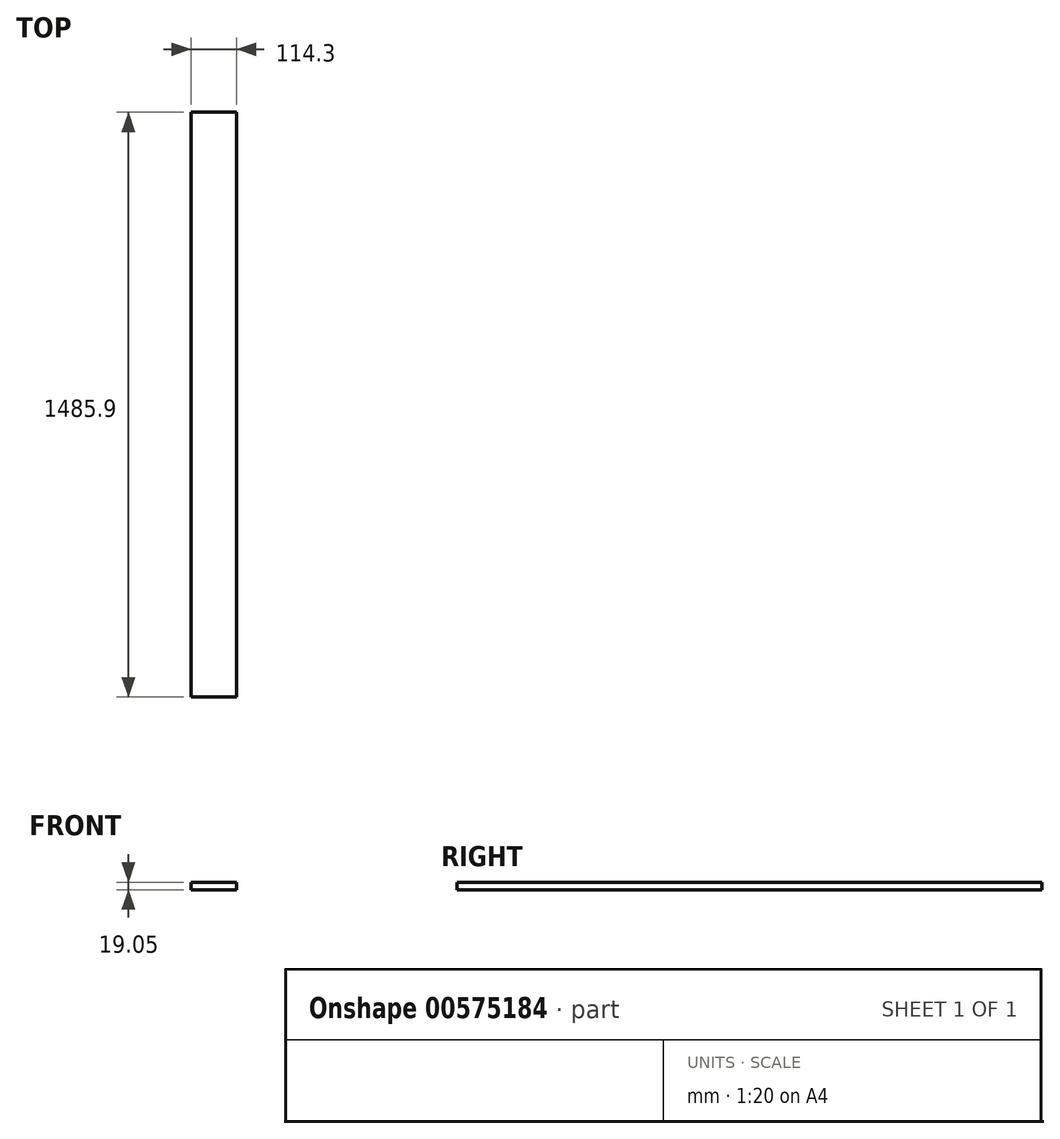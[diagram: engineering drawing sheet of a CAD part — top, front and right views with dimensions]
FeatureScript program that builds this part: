
annotation { "Feature Type Name" : "Feature", "Feature Type Description" : "" }
export const myFeature = defineFeature(function(context is Context, id is Id, definition is map)
    precondition{}
    {
        {
            var Q0;
            Q0=qCreatedBy(makeId("Top.planeOp"),FACE);
            var sketch = newSketch(context, id + "F0", { "sketchPlane" : qUnion([Q0])});
            skLineSegment(sketch, "E0.bottom", {"start": v(57.15, 742.95) * mm, "end": v(-57.15, 742.95) * mm});
            skLineSegment(sketch, "E0.top", {"start": v(57.15, -742.95) * mm, "end": v(-57.15, -742.95) * mm});
            skLineSegment(sketch, "E0.left", {"start": v(57.15, 742.95) * mm, "end": v(57.15, -742.95) * mm});
            skLineSegment(sketch, "E0.right", {"start": v(-57.15, 742.95) * mm, "end": v(-57.15, -742.95) * mm});
            skPoint(sketch, "E0.middle", {"position": v(0, 0) * mm});
            skSolve(sketch);
        }
        {
            var Q0;
            Q0=makeQuery(id+"F0.imprint","IMPRINT",FACE,{"disambiguationData":[TD([[makeQuery(id+"F0.imprint","IMPRINT",EDGE,{"derivedFrom":sQuery(id+"F0.wireOp",EDGE,"E0.bottom")}),1.0]])]});
            extrude(context, id + "F1", {"entities" : qUnion([Q0]), "depth" : 19.05 * mm, "offsetDistance" : 25.4 * mm});
        }
    });
